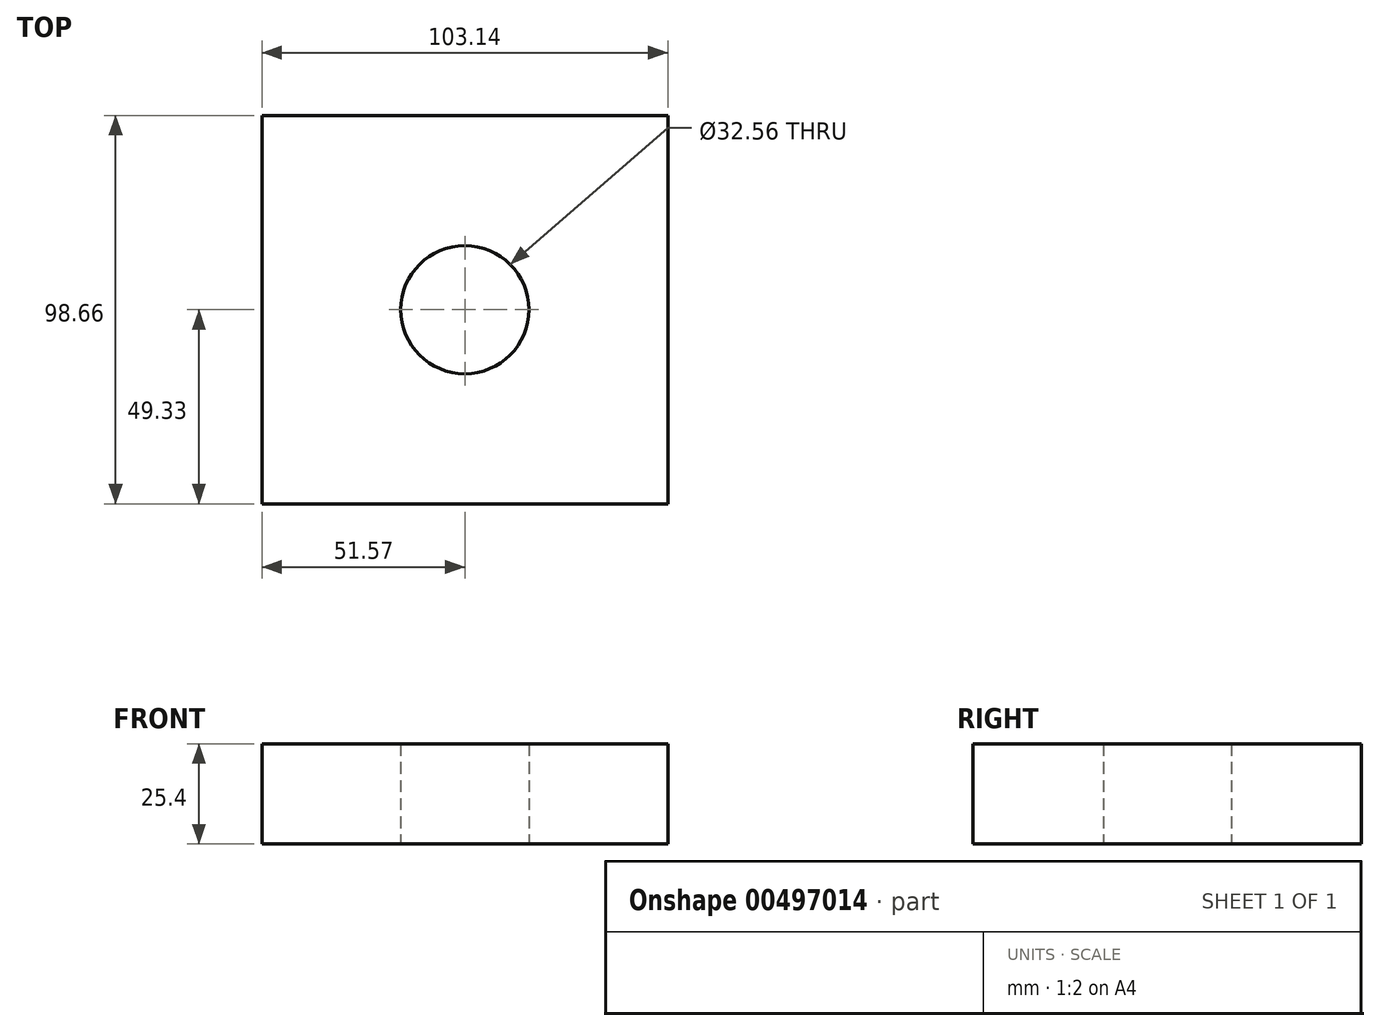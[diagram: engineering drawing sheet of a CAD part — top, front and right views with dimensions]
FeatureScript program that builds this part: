
annotation { "Feature Type Name" : "Feature", "Feature Type Description" : "" }
export const myFeature = defineFeature(function(context is Context, id is Id, definition is map)
    precondition{}
    {
        {
            var Q0;
            Q0=qCreatedBy(makeId("Top.planeOp"),FACE);
            var sketch = newSketch(context, id + "F0", { "sketchPlane" : qUnion([Q0])});
            skLineSegment(sketch, "E0.bottom", {"start": v(-51.57, 49.33) * mm, "end": v(51.57, 49.33) * mm});
            skLineSegment(sketch, "E0.top", {"start": v(-51.57, -49.33) * mm, "end": v(51.57, -49.33) * mm});
            skLineSegment(sketch, "E0.left", {"start": v(-51.57, 49.33) * mm, "end": v(-51.57, -49.33) * mm});
            skLineSegment(sketch, "E0.right", {"start": v(51.57, 49.33) * mm, "end": v(51.57, -49.33) * mm});
            skPoint(sketch, "E0.middle", {"position": v(0, 0) * mm});
            skCircle(sketch, "E1", {"center": v(0, 0) * mm, "radius": 16.28 * mm});
            skLineSegment(sketch, "E2", {"start": v(-32.18, 49.33) * mm, "end": v(-11.79, 49.33) * mm});
            skCircle(sketch, "E3", {"center": v(0, 0) * mm, "radius": 12.65 * mm});
            skSolve(sketch);
        }
        {
            var Q0;
            Q0=makeQuery(id+"F0.imprint","IMPRINT",FACE,{"disambiguationData":[TD([[makeQuery(id+"F0.imprint","IMPRINT",EDGE,{"derivedFrom":sQuery(id+"F0.wireOp",EDGE,"E0.bottom")}),-1.0]])]});
            extrude(context, id + "F1", {"entities" : qUnion([Q0]), "depth" : 25.4 * mm});
        }
        {
            var Q0;
            Q0=sQuery(id+"F0.wireOp",EDGE,"E1");
            extrude(context, id + "F2", {"bodyType" : ToolBodyType.SURFACE, "surfaceEntities" : qUnion([Q0]), "depth" : 46.48 * mm});
        }
        {
            var Q0;
            Q0=makeQuery(id+"F0.imprint","IMPRINT",FACE,{"disambiguationData":[TD([[makeQuery(id+"F0.imprint","IMPRINT",EDGE,{"derivedFrom":sQuery(id+"F0.wireOp",EDGE,"E0.bottom")}),-1.0]])]});
            extrude(context, id + "F3", {"entities" : qUnion([Q0]), "operationType" : NewBodyOperationType.ADD, "depth" : 25.4 * mm});
        }
    });
